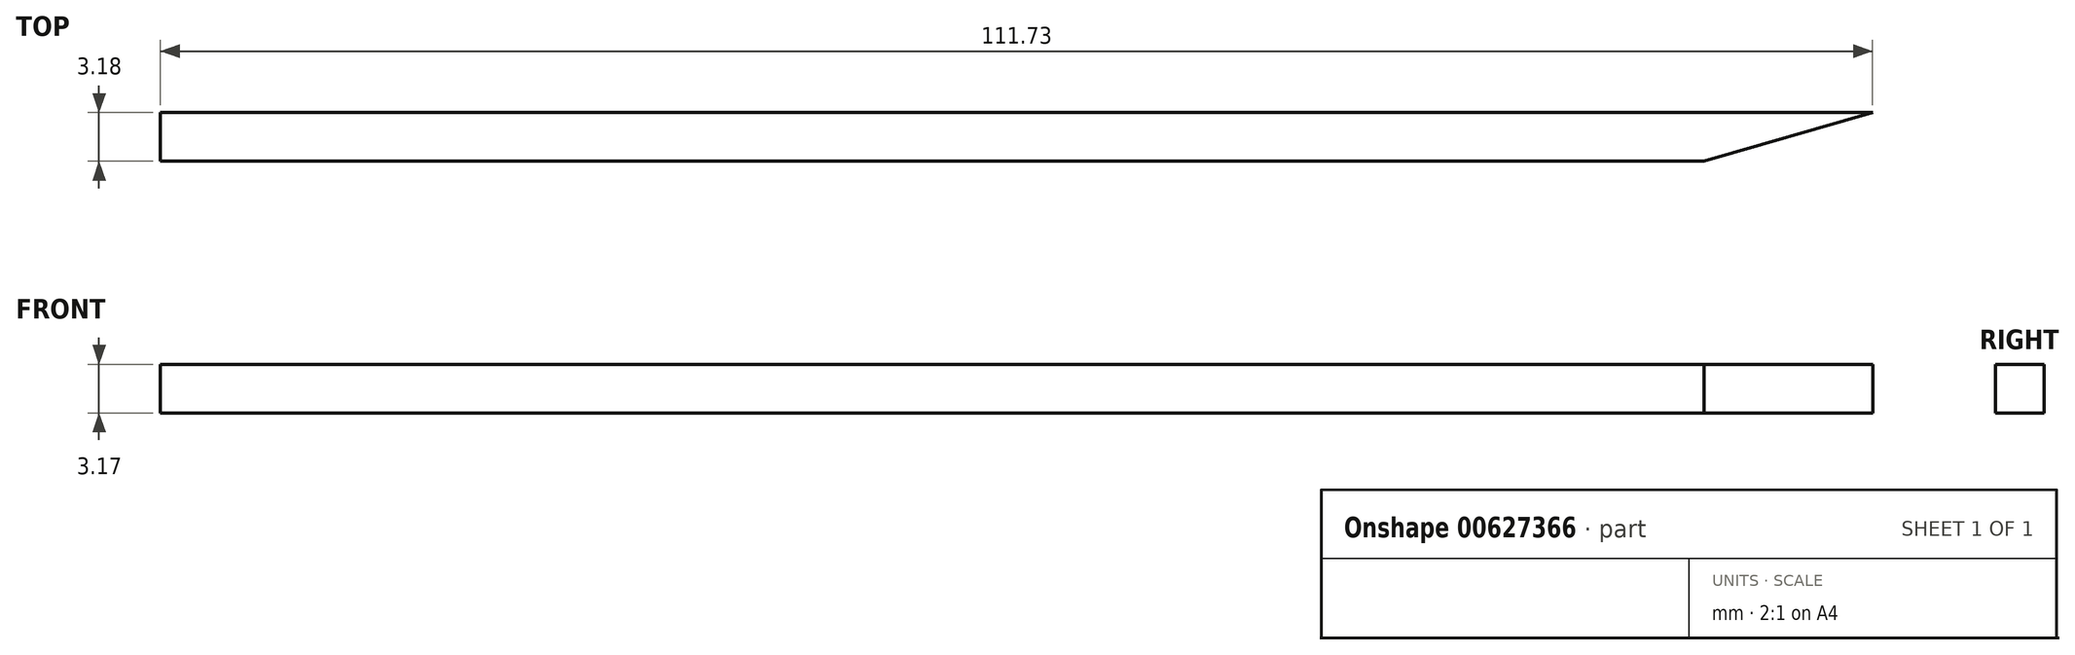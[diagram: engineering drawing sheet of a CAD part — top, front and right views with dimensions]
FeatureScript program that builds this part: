
annotation { "Feature Type Name" : "Feature", "Feature Type Description" : "" }
export const myFeature = defineFeature(function(context is Context, id is Id, definition is map)
    precondition{}
    {
        {
            var Q0;
            Q0=qCreatedBy(makeId("Top.planeOp"),FACE);
            var sketch = newSketch(context, id + "F0", { "sketchPlane" : qUnion([Q0])});
            skLineSegment(sketch, "E0", {"start": v(-52.71, 2.24) * mm, "end": v(59.02, 2.24) * mm});
            skLineSegment(sketch, "E1", {"start": v(-52.71, 2.24) * mm, "end": v(-52.71, -0.94) * mm});
            skLineSegment(sketch, "E2", {"start": v(-52.71, -0.94) * mm, "end": v(48.03, -0.94) * mm});
            skLineSegment(sketch, "E3", {"start": v(48.03, -0.94) * mm, "end": v(59.02, 2.24) * mm});
            skSolve(sketch);
        }
        {
            var Q0;
            Q0=makeQuery(id+"F0.imprint","IMPRINT",FACE,{"disambiguationData":[TD([[makeQuery(id+"F0.imprint","IMPRINT",EDGE,{"derivedFrom":sQuery(id+"F0.wireOp",EDGE,"E0")}),-1.0]])]});
            extrude(context, id + "F1", {"entities" : qUnion([Q0]), "depth" : 3.17 * mm, "offsetDistance" : 25.4 * mm});
        }
    });
